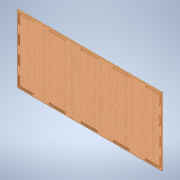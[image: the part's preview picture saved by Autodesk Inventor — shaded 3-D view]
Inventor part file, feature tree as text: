
AUTODESK INVENTOR PART (.ipt)
format: ipt  version: 2020.3 (Build 243373000, 373)  size: 225,792 bytes
history: native  units: mm
features: other x1, extrude x1
ambient origin geometry x8: Origin, YZ Plane, XZ Plane, XY Plane, X Axis, Y Axis, Z Axis, Center Point
bodies: Body1 (feature_tree)
feature tree (2):
  other  "Sólido1"
  extrude  "Extrusión1"  Depth=210.0mm
